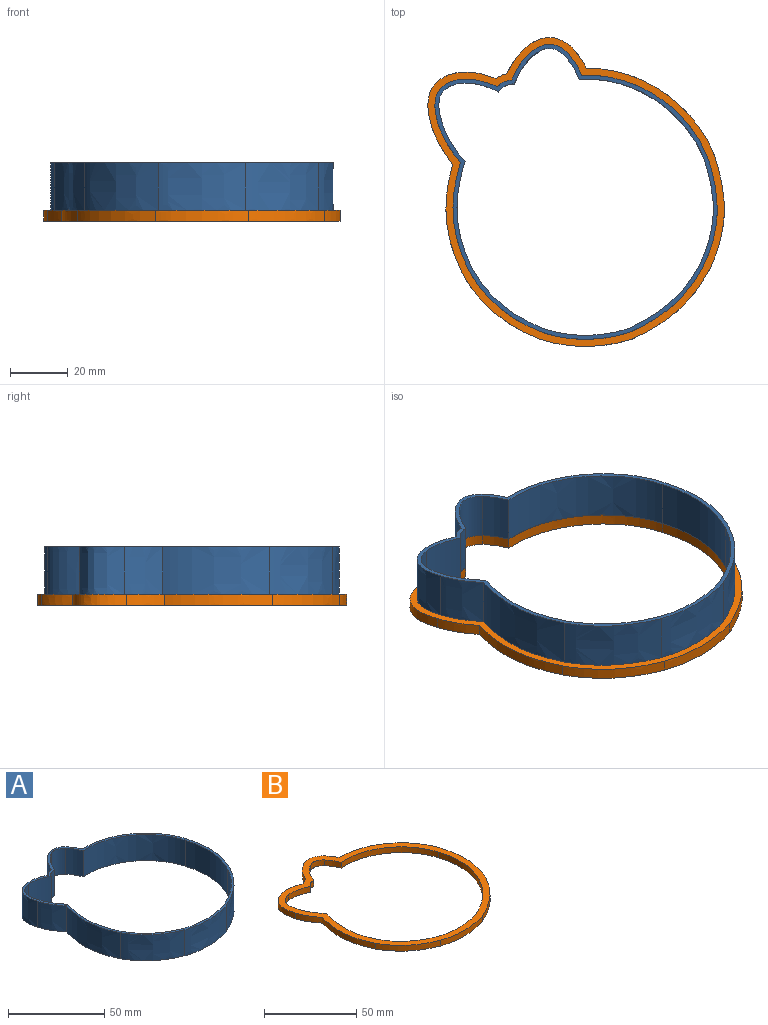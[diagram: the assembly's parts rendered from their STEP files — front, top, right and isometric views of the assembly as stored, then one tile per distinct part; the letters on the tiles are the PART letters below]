
ASSEMBLY  parts=2 mates=1
PART A: 28 faces, bbox 100.6x105x19.5 mm
  f0: plane 104.98x100.61mm, normal (0,0,1), area 436.7mm2, adj f2,f3,f4,f5,f6,f7,f8,f9
  f1: plane 104.98x100.61mm, normal (0,0,-1), area 436.7mm2, adj f2,f3,f4,f5,f6,f7,f8,f9
  f2: extruded ~44.59x31.88mm, area 972.8mm2, adj f0,f1,f3,f14
  f3: extruded ~16.51x7.42mm, area 144.7mm2, adj f0,f1,f2,f4
  f4: extruded ~16.51x10.4mm, area 190.3mm2, adj f0,f1,f3,f5
  f5: extruded ~16.51x11.31mm, area 246.6mm2, adj f0,f1,f4,f6
  f6: extruded ~16.51x4.85mm, area 91.7mm2, adj f0,f1,f5,f7
  f7: extruded ~16.51x13.63mm, area 232.1mm2, adj f0,f1,f6,f8
  f8: extruded ~16.51x15.38mm, area 327.1mm2, adj f0,f1,f7,f9
  f9: extruded ~16.51x13.25mm, area 255mm2, adj f0,f1,f8,f10
  f10: extruded ~36.95x16.51mm, area 628.5mm2, adj f0,f1,f9,f11
  f11: extruded ~25.59x21.79mm, area 567.3mm2, adj f0,f1,f10,f12
  f12: extruded ~30.26x16.51mm, area 508.4mm2, adj f0,f1,f11,f13
  f13: extruded ~25.05x22.18mm, area 563.3mm2, adj f0,f1,f12,f14
  f14: extruded ~34.83x16.51mm, area 592.9mm2, adj f0,f1,f2,f13
  f15: extruded ~44.14x30.87mm, area 957.8mm2, adj f0,f1,f16,f27
  f16: extruded ~16.51x7.92mm, area 153.1mm2, adj f0,f1,f15,f17
  f17: extruded ~16.51x8.74mm, area 160.5mm2, adj f0,f1,f16,f18
  f18: extruded ~16.51x11.46mm, area 245.9mm2, adj f0,f1,f17,f19
  f19: extruded ~16.51x5.29mm, area 103.9mm2, adj f0,f1,f18,f20
  f20: extruded ~16.51x13.87mm, area 237.4mm2, adj f0,f1,f19,f21
  f21: extruded ~16.51x13.61mm, area 288.4mm2, adj f0,f1,f20,f22
  f22: extruded ~16.51x13.32mm, area 258.1mm2, adj f0,f1,f21,f23
  f23: extruded ~36.68x16.51mm, area 624mm2, adj f0,f1,f22,f24
  f24: extruded ~24.84x21.13mm, area 550.4mm2, adj f0,f1,f23,f25
  f25: extruded ~29.29x16.51mm, area 492mm2, adj f0,f1,f24,f26
  f26: extruded ~24.34x21.54mm, area 547.1mm2, adj f0,f1,f25,f27
  f27: extruded ~33.82x16.51mm, area 575.6mm2, adj f0,f1,f15,f26
PART B: 28 faces, bbox 105.5x109.8x6.8 mm
  f0: plane 109.82x105.46mm, normal (0,0,1), area 1239.6mm2, adj f2,f3,f4,f5,f6,f7,f8,f9
  f1: plane 109.82x105.46mm, normal (0,0,-1), area 1239.6mm2, adj f2,f3,f4,f5,f6,f7,f8,f9
  f2: extruded ~45.4x33.66mm, area 230.7mm2, adj f0,f1,f3,f14
  f3: extruded ~6.58x4.33mm, area 30.1mm2, adj f0,f1,f2,f4
  f4: extruded ~13.34x4.06mm, area 56mm2, adj f0,f1,f3,f5
  f5: extruded ~11.26x9.83mm, area 58mm2, adj f0,f1,f4,f6
  f6: extruded ~3.81x3.69mm, area 15.6mm2, adj f0,f1,f5,f7
  f7: extruded ~13.54x3.81mm, area 52.8mm2, adj f0,f1,f6,f8
  f8: extruded ~18.53x10.04mm, area 91.3mm2, adj f0,f1,f7,f9
  f9: extruded ~13.1x7.32mm, area 57.5mm2, adj f0,f1,f8,f10
  f10: extruded ~37.47x5.52mm, area 147mm2, adj f0,f1,f9,f11
  f11: extruded ~26.92x22.97mm, area 137.9mm2, adj f0,f1,f10,f12
  f12: extruded ~31.99x3.81mm, area 124mm2, adj f0,f1,f11,f13
  f13: extruded ~26.32x23.31mm, area 136.6mm2, adj f0,f1,f12,f14
  f14: extruded ~36.63x5.48mm, area 143.9mm2, adj f0,f1,f2,f13
  f15: extruded ~44.14x30.87mm, area 221mm2, adj f0,f1,f16,f27
  f16: extruded ~7.92x4.74mm, area 35.3mm2, adj f0,f1,f15,f17
  f17: extruded ~8.74x3.81mm, area 37mm2, adj f0,f1,f16,f18
  f18: extruded ~11.46x9.02mm, area 56.8mm2, adj f0,f1,f17,f19
  f19: extruded ~5.29x3.81mm, area 24mm2, adj f0,f1,f18,f20
  f20: extruded ~13.87x3.81mm, area 54.8mm2, adj f0,f1,f19,f21
  f21: extruded ~13.61x6.88mm, area 66.5mm2, adj f0,f1,f20,f22
  f22: extruded ~13.32x7.95mm, area 59.6mm2, adj f0,f1,f21,f23
  f23: extruded ~36.68x5.11mm, area 144mm2, adj f0,f1,f22,f24
  f24: extruded ~24.84x21.13mm, area 127mm2, adj f0,f1,f23,f25
  f25: extruded ~29.29x3.81mm, area 113.5mm2, adj f0,f1,f24,f26
  f26: extruded ~24.34x21.54mm, area 126.3mm2, adj f0,f1,f25,f27
  f27: extruded ~33.82x5.04mm, area 132.8mm2, adj f0,f1,f15,f26
PLACE A t=(123.12,11.55,3.81)mm
PLACE B at identity
MATE fastened A.f1 <-> B.f0  axis (0,0,1) through (69.48,25.53,3.81)mm
